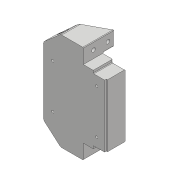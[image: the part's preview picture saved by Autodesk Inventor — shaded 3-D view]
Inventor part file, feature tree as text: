
AUTODESK INVENTOR PART (.ipt)
format: ipt  version: 2018 (Build 220112000, 112)  size: 2,393,088 bytes
history: native  units: mm
features: sketch x51, projected_geometry x44, extrude x43, fillet x19, hole x6, chamfer x5, mirror x3, other x2, plane x2, revolve x1, shell x1, pattern_circular x1, loft x1
ambient origin geometry x8: Origin, YZ Plane, XZ Plane, XY Plane, X Axis, Y Axis, Z Axis, Center Point
bodies: Solid1 (feature_tree), Solid2 (feature_tree), Solid3 (feature_tree)
feature tree (179):
  extrude  "Extrusion1"  Depth=45.0mm
  extrude  "Extrusion2"  Depth=2.25mm
  hole  "Hole1"  [1 undecoded]
  hole  "Hole2"  [1 undecoded]
  fillet  "Fillet1"  Radius=14.0mm
  extrude  "Extrusion3"  Depth=18.5mm
  extrude  "Extrusion4"  Depth=10.0mm
  extrude  "Extrusion5"  Depth=2.0mm
  extrude  "Extrusion6"  Depth=2.0mm
  hole  "Hole3"  [1 undecoded]
  extrude  "Extrusion7"  Depth=2.0mm
  extrude  "Extrusion8"  Depth=5.0mm TaperAngle=0.0deg
  extrude  "Extrusion9"  Depth=10.0mm
  extrude  "Extrusion10"  Depth=10.0mm
  extrude  "Extrusion11"  Depth=14.5mm
  extrude  "Extrusion12"  Depth=14.5mm
  extrude  "Extrusion13"  Depth=5.0mm
  extrude  "Extrusion14"  Depth=2.25mm
  extrude  "Extrusion15"  Depth=5.0mm
  extrude  "Extrusion16"  Depth=9.0mm
  extrude  "Extrusion17"  Depth=1.0mm
  chamfer  "Chamfer1"  Distance=1.0mm
  fillet  "Fillet7"  Radius=20.7mm
  fillet  "Fillet8"  Radius=32.0mm
  mirror  "Mirror1"
  extrude  "Extrusion18"  Depth=1.0mm TaperAngle=0.0deg
  extrude  "Extrusion19"  Depth=8.0mm
  extrude  "Extrusion20"  Depth=0.2mm TaperAngle=0.0deg
  extrude  "Extrusion21"  Depth=0.5mm TaperAngle=0.0deg
  extrude  "Extrusion22"  Depth=3.0mm TaperAngle=0.0deg
  extrude  "Extrusion23"  Depth=0.2mm TaperAngle=0.0deg
  extrude  "Extrusion24"  Depth=2.0mm TaperAngle=45.0deg
  sketch  "Sketch35"  dims[d91=8.0mm d92=0.0mm d93=3.0mm d94=0.0mm]
  other  "Work Axis1"
  revolve  "Revolution1"  [1 undecoded]
  extrude  "Extrusion25"  Depth=4.0mm TaperAngle=0.0deg
  extrude  "Extrusion26"  Depth=19.2mm TaperAngle=0.0deg
  shell  "Shell1"  Thickness=52.1mm
  extrude  "Extrusion27"  Depth=9.0mm
  extrude  "Extrusion28"  Depth=25.0mm
  chamfer  "Chamfer4"  Distance=6.9mm
  chamfer  "Chamfer5"  Distance=2.5mm
  extrude  "Extrusion29"  TaperAngle=90.0deg  [1 undecoded]
  pattern_circular  "Circular Pattern1"  Count=2  [1 undecoded]
  fillet  "Fillet11"  Radius=20.0mm
  fillet  "Fillet12"  Radius=20.0mm
  fillet  "Fillet13"  Radius=6.0mm
  fillet  "Fillet14"  Radius=40.0mm
  chamfer  "Chamfer6"  Distance=40.0mm
  hole  "Hole6"  [1 undecoded]
  extrude  "Extrusion30"  Depth=10.0mm
  fillet  "Fillet15"  Radius=10.0mm
  extrude  "Extrusion31"  Depth=1.0mm TaperAngle=0.0deg
  plane  "Work Plane1"
  loft  "Loft1"
  hole  "Hole8"  [1 undecoded]
  extrude  "Extrusion35"  Depth=1.0mm
  chamfer  "Chamfer7"  Distance=50.0mm
  fillet  "Fillet20"  Radius=50.0mm
  extrude  "Extrusion36"  Depth=2.0mm TaperAngle=45.0deg
  extrude  "Extrusion37"  Depth=1.0mm
  extrude  "Extrusion38"  Depth=1.0mm
  extrude  "Extrusion39"  Depth=1.0mm
  extrude  "Extrusion40"  Depth=1.0mm
  extrude  "Extrusion41"  Depth=1.0mm
  extrude  "Extrusion47"  Depth=1.0mm
  extrude  "Extrusion48"  Depth=1.0mm
  extrude  "Extrusion49"  Depth=1.0mm TaperAngle=0.0deg
  fillet  "Fillet33"  Radius=1.0mm
  extrude  "Extrusion50"  Depth=2.0mm TaperAngle=0.0deg
  hole  "Hole11"  [1 undecoded]
  fillet  "Fillet35"  Radius=150.0mm
  plane  "Work Plane3"
  mirror  "Mirror4"
  fillet  "Fillet34"  [1 undecoded]
  fillet  "Fillet36"  [1 undecoded]
  fillet  "Fillet37"  Radius=45.0mm
  fillet  "Fillet38"  Radius=1.0mm
  fillet  "Fillet39"  Radius=1.0mm
  fillet  "Fillet40"  Radius=30.0mm
  extrude  "Extrusion51"  Depth=1.0mm TaperAngle=0.0deg
  mirror  "Mirror5"
  fillet  "Fillet41"  Radius=118.0mm
  fillet  "Fillet42"  Radius=120.0mm
  sketch  "Sketch1"  dims[d0=24.5mm d1=45.0mm]
  sketch  "Sketch2"  dims[d2=1.95mm d3=0.0mm d4=2.25mm]
  projected_geometry  "Projected Loop1"
  sketch  "Sketch3"  dims[d5=20.0mm d6=2.25mm]
  projected_geometry  "Projected Loop2"
  sketch  "Sketch4"  dims[d7=5.25mm d8=5.25mm d9=14.0mm]
  projected_geometry  "Projected Loop3"
  sketch  "Sketch5"  dims[d10=5.25mm d11=18.5mm]
  projected_geometry  "Projected Loop4"
  sketch  "Sketch6"  dims[d12=10.0mm d13=0.0mm d14=20.5mm]
  projected_geometry  "Projected Loop5"
  sketch  "Sketch7"  dims[d15=2.0mm d16=2.195mm]
  projected_geometry  "Projected Loop6"
  sketch  "Sketch8"  dims[d17=2.0mm]
  projected_geometry  "Projected Loop7"
  sketch  "Sketch9"  dims[d18=2.4mm d19=6.0mm d20=4.4mm d21=2.0mm d22=90.0deg d23=8.0mm d24=20.594885mm d25=20.5mm]
  projected_geometry  "Projected Loop8"
  projected_geometry  "Projected Loop9"
  sketch  "Sketch10"  dims[d26=26.65mm d27=2.0mm]
  projected_geometry  "Projected Loop10"
  projected_geometry  "Projected Loop11"
  sketch  "Sketch11"  dims[d28=2.0mm]
  projected_geometry  "Projected Loop12"
  sketch  "Sketch12"  dims[d29=2.4mm d30=6.0mm d31=4.4mm d32=2.0mm d33=90.0deg d34=8.0mm d35=20.594885mm d36=0.5mm]
  sketch  "Sketch13"  dims[d37=18.0mm d38=5.0mm d39=0.0mm]
  sketch  "Sketch14"  dims[d41=10.0mm d42=0.0mm d43=24.5mm]
  projected_geometry  "Projected Loop13"
  sketch  "Sketch15"  dims[d44=1.15mm d45=0.0mm d46=10.0mm]
  sketch  "Sketch16"  dims[d47=21.0mm d48=14.5mm]
  projected_geometry  "Projected Loop14"
  sketch  "Sketch17"  dims[d49=20.0mm d50=14.5mm]
  projected_geometry  "Projected Loop15"
  sketch  "Sketch18"  dims[d51=24.5mm d52=5.0mm]
  projected_geometry  "Projected Loop16"
  sketch  "Sketch19"  dims[d53=5.0mm d54=2.25mm]
  projected_geometry  "Projected Loop17"
  sketch  "Sketch20"  dims[d55=2.25mm d56=5.0mm]
  projected_geometry  "Projected Loop18"
  sketch  "Sketch22"  dims[d57=5.0mm d58=9.0mm]
  sketch  "Sketch25"  dims[d59=14.75mm d60=4.0mm d61=1.0mm d62=0.0mm d63=20.7mm]
  sketch  "Sketch27"  dims[d64=2.4mm d65=6.0mm d66=4.4mm d67=2.0mm d68=90.0deg d69=8.0mm d70=20.594885mm d72=32.0mm]
  projected_geometry  "Projected Loop22"
  sketch  "Sketch28"  dims[d73=5.0mm d74=0.0mm d75=1.0mm d76=0.0mm]
  projected_geometry  "Projected Loop23"
  sketch  "Sketch29"  dims[d77=12.25mm d78=0.0mm d80=8.0mm]
  projected_geometry  "Projected Loop24"
  sketch  "Sketch30"  dims[d81=4.5mm d82=0.0mm d84=0.2mm d85=0.0mm]
  projected_geometry  "Projected Loop25"
  sketch  "Sketch33"  dims[d86=21.0mm d87=0.5mm d88=0.0mm]
  projected_geometry  "Projected Loop26"
  sketch  "Sketch36"  dims[d95=5.0mm d96=0.0mm d98=0.2mm d99=0.0mm]
  projected_geometry  "Projected Loop27"
  sketch  "Sketch37"  dims[d100=0.2mm d101=0.0mm d102=2.5mm d103=2.0mm d104=45.0deg]
  projected_geometry  "Projected Loop28"
  sketch  "Sketch38"  dims[d105=1.5mm d114=0.5mm]
  projected_geometry  "Projected Loop29"
  projected_geometry  "Projected Loop30"
  projected_geometry  "Projected Loop31"
  projected_geometry  "Projected Loop32"
  sketch  "Sketch39"  dims[d115=22.55mm d116=0.0mm d128=4.0mm d129=0.0mm]
  projected_geometry  "Projected Loop33"
  projected_geometry  "Projected Loop34"
  sketch  "Sketch40"  dims[d130=4.0mm d131=0.0mm d132=19.2mm d133=0.0mm d134=52.1mm]
  projected_geometry  "Projected Loop35"
  sketch  "Sketch41"  dims[d135=6.8mm d136=0.0mm d137=9.0mm]
  projected_geometry  "Projected Loop36"
  sketch  "Sketch42"  dims[d138=9.0mm d139=25.0mm d140=6.9mm d141=0.0mm]
  sketch  "Sketch43"  dims[d142=5.2mm]
  projected_geometry  "Projected Loop37"
  sketch  "Sketch49"  dims[d143=5.2mm]
  other  "Edges1"
  sketch  "Sketch50"  dims[d144=5.2mm]
  sketch  "Sketch51"  dims[d145=5.2mm d146=2.5mm d147=0.0mm]
  sketch  "Sketch52"  dims[d148=5.0mm d149=90.0deg]
  projected_geometry  "Projected Loop40"
  sketch  "Sketch53"  dims[d150=5.0mm]
  sketch  "Sketch55"  dims[d151=105.0mm]
  projected_geometry  "Projected Loop41"
  sketch  "Sketch56"  dims[d152=105.0mm]
  projected_geometry  "Projected Loop42"
  projected_geometry  "Projected Loop43"
  sketch  "Sketch57"  dims[d153=5.0mm d154=0.0mm]
  sketch  "Sketch58"  dims[d156=12.8mm]
  sketch  "Sketch66"  dims[d157=12.8mm]
  sketch  "Sketch67"  dims[d158=12.8mm]
  projected_geometry  "Projected Loop49"
  sketch  "Sketch68"  dims[d159=12.8mm d160=20.0mm d161=20.0mm d162=20.0mm d163=6.0mm d164=40.0mm d165=0.0mm]
  projected_geometry  "Projected Loop50"
  projected_geometry  "Projected Loop51"
  sketch  "Sketch69"  dims[d166=8.0mm d167=40.0mm d168=0.0mm]
  projected_geometry  "Projected Loop52"
  sketch  "Sketch70"  dims[d169=40.0mm d170=0.0mm d178=5.1mm d179=2.45mm d180=45.0deg]
  sketch  "Sketch71"  dims[d181=4.1mm d182=2.45mm d183=45.0deg d184=10.0mm d185=10.0mm d186=40.0mm d187=0.0mm d188=40.0mm d189=360.0deg d191=5.1mm d192=25.0mm d193=50.0mm d194=50.0mm d195=5.0mm d196=2.0mm d197=45.0deg d198=110.0mm d199=77.781746mm d200=77.781746mm d201=4.134mm d202=10.0mm d203=12.6mm d204=2.0mm d205=90.0deg d206=14.2mm d207=20.594885mm d208=11.0mm d209=11.0mm d210=11.0mm d211=11.0mm d212=45.0mm d213=0.0mm d214=1.0mm d215=2.0mm d216=0.0mm d236=45.0mm d237=150.0mm d238=0.0mm d239=90.0deg d240=0.0mm d241=90.0deg d242=4.134mm d243=10.0mm d244=4.0mm d245=2.0mm d246=90.0deg d247=14.2mm d248=20.594885mm d249=45.0mm d250=0.0mm d251=1.0mm d252=2.0mm d253=45.0deg d254=1.0mm d255=30.0mm d256=0.0mm d257=25.0mm d258=0.0mm d270=118.0mm d271=120.0mm d272=21.109127mm d273=21.109127mm d274=4.0mm d275=0.0mm d276=16.0mm d277=0.5mm d278=30.0mm d279=0.0mm d280=30.0mm d281=0.0mm d284=30.0mm d285=0.0mm d323=48.0mm d324=40.0mm d325=172.0mm d326=26.0mm d327=26.0mm d328=8.5mm d329=0.0mm d330=0.0mm d331=20.0mm d332=0.0mm d334=3.0mm d335=18.0mm d336=20.0mm d337=0.0mm d338=2.0mm d339=2.0mm d340=3.175mm d341=0.0mm d342=1.0mm d343=25.4mm d344=18.0mm d345=12.7mm d346=6.756mm d347=6.0mm d348=11.113mm d349=64.0mm d350=14.3117mm d351=8.0mm d352=20.594885mm d353=1.0mm d354=1.25mm d355=5.0mm d356=2.0mm d357=1.0mm d358=1.0mm d359=22.0mm d361=5.0mm d362=0.0mm d363=1.0mm d364=1.0mm]
  projected_geometry  "Projected Loop53"
  projected_geometry  "Project Cut Edges1"
note: 11 required parameter values undecoded (feature->parameter linkage not recoverable at this tier; creation-order binding heuristic only, values carry confidence <= 0.55)